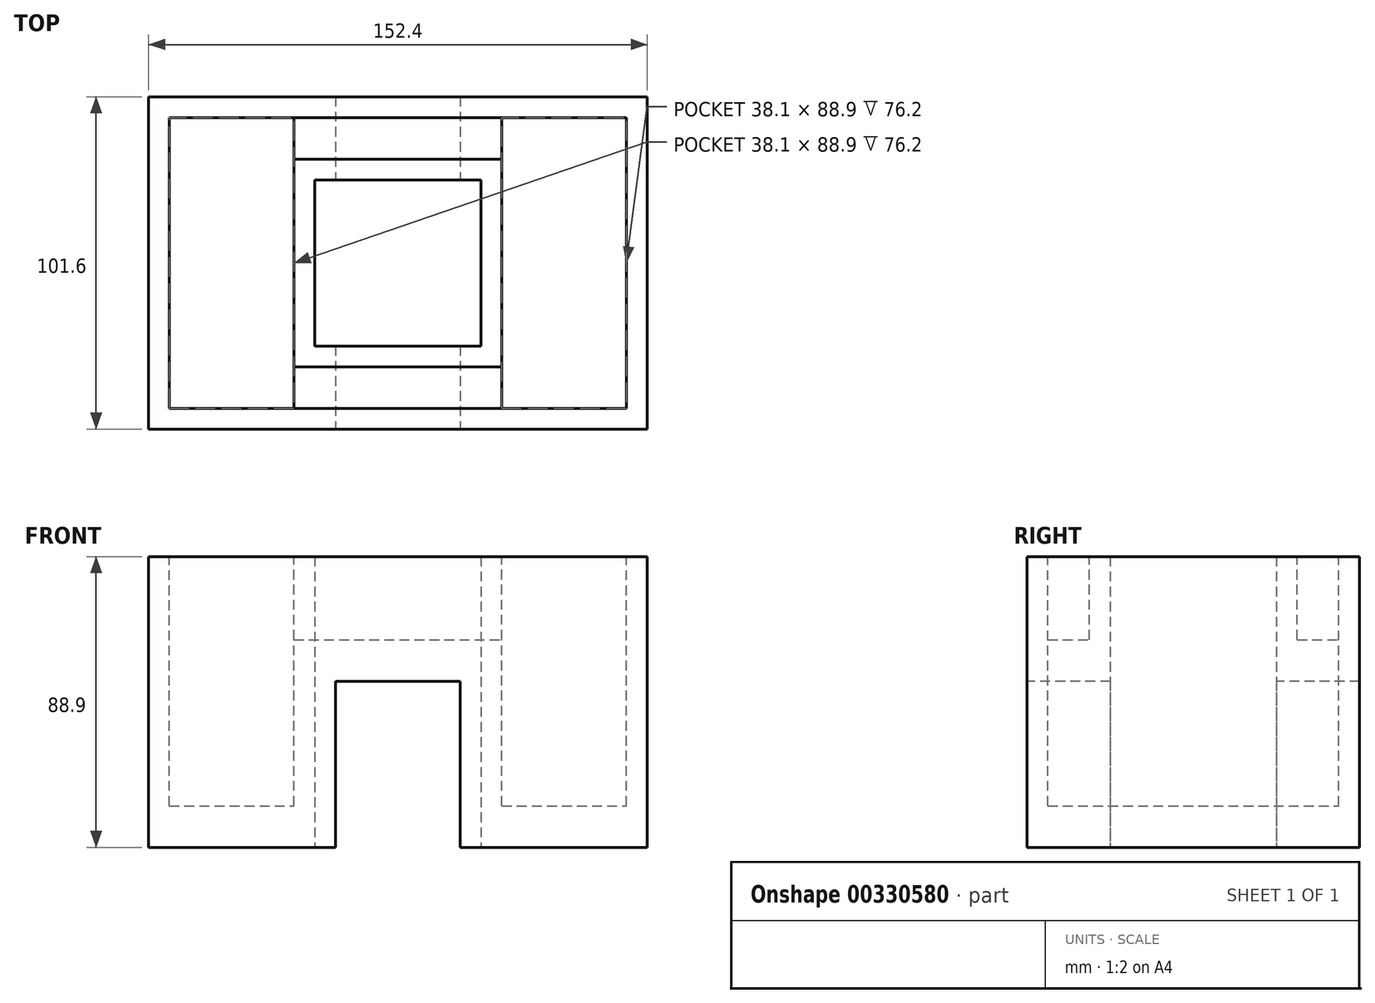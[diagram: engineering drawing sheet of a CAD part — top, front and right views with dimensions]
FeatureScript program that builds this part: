
annotation { "Feature Type Name" : "Feature", "Feature Type Description" : "" }
export const myFeature = defineFeature(function(context is Context, id is Id, definition is map)
    precondition{}
    {
        {
            var Q0;
            Q0=qCreatedBy(makeId("Top.planeOp"),FACE);
            var sketch = newSketch(context, id + "F0", { "sketchPlane" : qUnion([Q0])});
            skLineSegment(sketch, "E0.bottom", {"start": v(-9.96, -51.78) * mm, "end": v(-60.76, -51.78) * mm});
            skLineSegment(sketch, "E0.top", {"start": v(-9.96, 49.82) * mm, "end": v(-60.76, 49.82) * mm});
            skLineSegment(sketch, "E0.left", {"start": v(-9.96, -51.78) * mm, "end": v(-9.96, 49.82) * mm});
            skLineSegment(sketch, "E0.right", {"start": v(-60.76, -51.78) * mm, "end": v(-60.76, 49.82) * mm});
            skLineSegment(sketch, "E1.bottom", {"start": v(-9.96, -51.78) * mm, "end": v(40.84, -51.78) * mm});
            skLineSegment(sketch, "E1.top", {"start": v(-9.96, -26.38) * mm, "end": v(40.84, -26.38) * mm});
            skLineSegment(sketch, "E1.left", {"start": v(-9.96, -51.78) * mm, "end": v(-9.96, -26.38) * mm});
            skLineSegment(sketch, "E1.right", {"start": v(40.84, -51.78) * mm, "end": v(40.84, -26.38) * mm});
            skLineSegment(sketch, "E2.bottom", {"start": v(-9.96, 49.82) * mm, "end": v(40.84, 49.82) * mm});
            skLineSegment(sketch, "E2.top", {"start": v(-9.96, 24.42) * mm, "end": v(40.84, 24.42) * mm});
            skLineSegment(sketch, "E2.left", {"start": v(-9.96, 49.82) * mm, "end": v(-9.96, 24.42) * mm});
            skLineSegment(sketch, "E2.right", {"start": v(40.84, 49.82) * mm, "end": v(40.84, 24.42) * mm});
            skLineSegment(sketch, "E3.bottom", {"start": v(40.84, 49.82) * mm, "end": v(40.84, 49.82) * mm});
            skLineSegment(sketch, "E3.top", {"start": v(40.84, -51.78) * mm, "end": v(40.84, -51.78) * mm});
            skLineSegment(sketch, "E3.left", {"start": v(40.84, 49.82) * mm, "end": v(40.84, -51.78) * mm});
            skLineSegment(sketch, "E4.bottom", {"start": v(40.84, -51.78) * mm, "end": v(91.64, -51.78) * mm});
            skLineSegment(sketch, "E4.top", {"start": v(40.84, 49.82) * mm, "end": v(91.64, 49.82) * mm});
            skLineSegment(sketch, "E4.left", {"start": v(40.84, -51.78) * mm, "end": v(40.84, 49.82) * mm});
            skLineSegment(sketch, "E4.right", {"start": v(91.64, -51.78) * mm, "end": v(91.64, 49.82) * mm});
            skSolve(sketch);
        }
        {
            var Q0;
            Q0 = qSketchRegion(id + "F0", true);
            extrude(context, id + "F1", {"entities" : qUnion([Q0]), "depth" : 88.9 * mm});
        }
        {
            var Q0;
            Q0=makeQuery(id+"F1.opExtrude","CAP_FACE",FACE,{"disambiguationData":[OSD([sQuery(id+"F0.wireOp",EDGE,"E0.bottom"),sQuery(id+"F0.wireOp",EDGE,"E0.top"),sQuery(id+"F0.wireOp",EDGE,"E0.left"),sQuery(id+"F0.wireOp",EDGE,"E0.right"),sQuery(id+"F0.wireOp",EDGE,"E1.bottom"),sQuery(id+"F0.wireOp",EDGE,"E1.top"),sQuery(id+"F0.wireOp",EDGE,"E2.bottom"),sQuery(id+"F0.wireOp",EDGE,"E2.top"),sQuery(id+"F0.wireOp",EDGE,"E4.bottom"),sQuery(id+"F0.wireOp",EDGE,"E4.top"),sQuery(id+"F0.wireOp",EDGE,"E4.left"),sQuery(id+"F0.wireOp",EDGE,"E4.right")])],"isStart":false});
            var sketch = newSketch(context, id + "F2", { "sketchPlane" : qUnion([Q0])});
            skLineSegment(sketch, "E5.bottom", {"start": v(-54.4, -45.43) * mm, "end": v(-16.3, -45.43) * mm});
            skLineSegment(sketch, "E5.top", {"start": v(-54.4, 43.47) * mm, "end": v(-16.3, 43.47) * mm});
            skLineSegment(sketch, "E5.left", {"start": v(-54.4, -45.43) * mm, "end": v(-54.4, 43.47) * mm});
            skLineSegment(sketch, "E5.right", {"start": v(-16.3, -45.43) * mm, "end": v(-16.3, 43.47) * mm});
            skLineSegment(sketch, "E6.bottom", {"start": v(-16.3, -45.43) * mm, "end": v(47.2, -45.43) * mm});
            skLineSegment(sketch, "E6.top", {"start": v(-16.3, -32.73) * mm, "end": v(47.2, -32.73) * mm});
            skLineSegment(sketch, "E6.left", {"start": v(-16.3, -45.43) * mm, "end": v(-16.3, -32.73) * mm});
            skLineSegment(sketch, "E6.right", {"start": v(47.2, -45.43) * mm, "end": v(47.2, -32.73) * mm});
            skLineSegment(sketch, "E7.bottom", {"start": v(47.2, -45.43) * mm, "end": v(85.3, -45.43) * mm});
            skLineSegment(sketch, "E7.top", {"start": v(47.2, 43.47) * mm, "end": v(85.3, 43.47) * mm});
            skLineSegment(sketch, "E7.left", {"start": v(47.2, -45.43) * mm, "end": v(47.2, 43.47) * mm});
            skLineSegment(sketch, "E7.right", {"start": v(85.3, -45.43) * mm, "end": v(85.3, 43.47) * mm});
            skLineSegment(sketch, "E8.bottom", {"start": v(-16.3, 43.47) * mm, "end": v(47.2, 43.47) * mm});
            skLineSegment(sketch, "E8.top", {"start": v(-16.3, 30.77) * mm, "end": v(47.2, 30.77) * mm});
            skLineSegment(sketch, "E8.left", {"start": v(-16.3, 43.47) * mm, "end": v(-16.3, 30.77) * mm});
            skLineSegment(sketch, "E8.right", {"start": v(47.2, 43.47) * mm, "end": v(47.2, 30.77) * mm});
            skSolve(sketch);
        }
        {
            var Q0;
            Q0=makeQuery(id+"F2.imprint","IMPRINT",FACE,{"disambiguationData":[TD([[makeQuery(id+"F2.imprint","IMPRINT",EDGE,{"derivedFrom":sQuery(id+"F2.wireOp",EDGE,"E5.bottom")}),1.0]])]});
            var Q1;
            {var subQ3=sQuery(id+"F2.wireOp",EDGE,"E7.bottom");Q1=makeQuery(id+"F2.imprint","IMPRINT",FACE,{"disambiguationData":[TD([[makeQuery(id+"F2.imprint","IMPRINT",EDGE,{"derivedFrom":subQ3}),1.0]])]});}
            extrude(context, id + "F3", {"entities" : qUnion([Q0, Q1]), "operationType" : NewBodyOperationType.REMOVE, "oppositeDirection" : true, "depth" : 76.2 * mm});
        }
        {
            var Q0;
            {var subQ0=sQuery(id+"F2.wireOp",EDGE,"E6.bottom");Q0=makeQuery(id+"F2.imprint","IMPRINT",FACE,{"disambiguationData":[TD([[makeQuery(id+"F2.imprint","IMPRINT",EDGE,{"derivedFrom":subQ0}),1.0]])]});}
            var Q1;
            Q1=makeQuery(id+"F2.imprint","IMPRINT",FACE,{"disambiguationData":[TD([[makeQuery(id+"F2.imprint","IMPRINT",EDGE,{"derivedFrom":sQuery(id+"F2.wireOp",EDGE,"E8.bottom")}),-1.0]])]});
            extrude(context, id + "F4", {"entities" : qUnion([Q0, Q1]), "operationType" : NewBodyOperationType.REMOVE, "oppositeDirection" : true, "depth" : 25.4 * mm});
        }
        {
            var Q0;
            Q0=makeQuery(id+"F1.opExtrude","SWEPT_FACE",FACE,{"disambiguationData":[OSD([sQuery(id+"F0.wireOp",EDGE,"E0.bottom"),sQuery(id+"F0.wireOp",EDGE,"E1.bottom"),sQuery(id+"F0.wireOp",EDGE,"E4.bottom")])]});
            var sketch = newSketch(context, id + "F5", { "sketchPlane" : qUnion([Q0])});
            skLineSegment(sketch, "E9.right", {"start": v(-3.6, 0) * mm, "end": v(-3.6, 50.8) * mm});
            skLineSegment(sketch, "E10.bottom", {"start": v(-3.6, 50.8) * mm, "end": v(34.5, 50.8) * mm});
            skLineSegment(sketch, "E10.top", {"start": v(-3.6, 0) * mm, "end": v(34.5, 0) * mm});
            skLineSegment(sketch, "E10.right", {"start": v(34.5, 50.8) * mm, "end": v(34.5, 0) * mm});
            skSolve(sketch);
        }
        {
            var Q0;
            Q0 = qSketchRegion(id + "F5", true);
            extrude(context, id + "F6", {"entities" : qUnion([Q0]), "operationType" : NewBodyOperationType.REMOVE, "oppositeDirection" : true, "depth" : 110.74 * mm});
        }
    });
